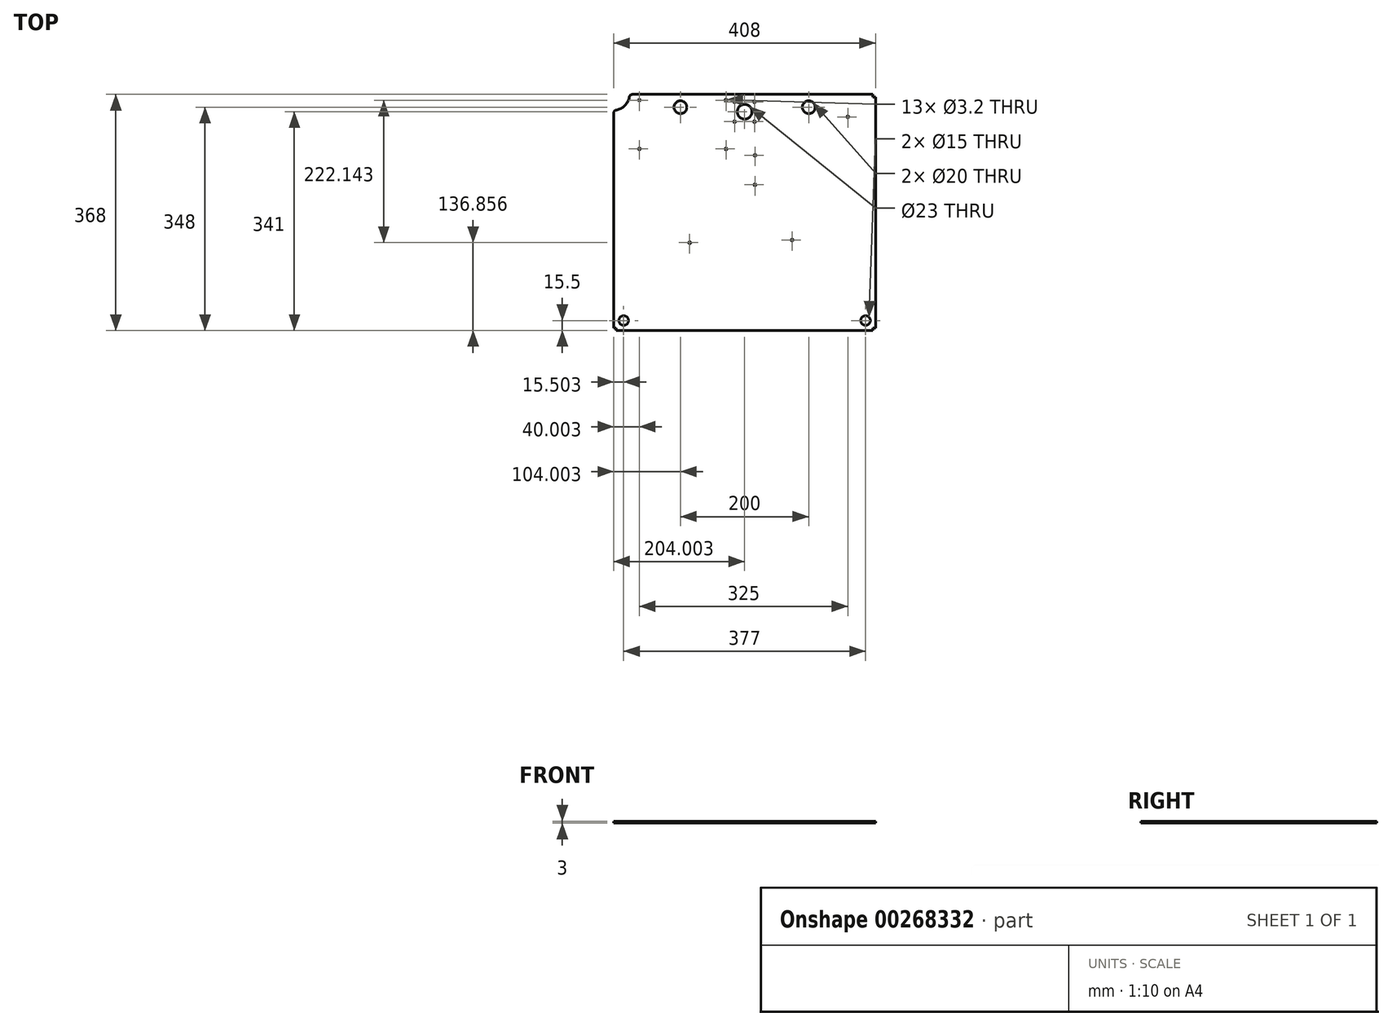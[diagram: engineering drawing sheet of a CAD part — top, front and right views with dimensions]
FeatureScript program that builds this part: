
annotation { "Feature Type Name" : "Feature", "Feature Type Description" : "" }
export const myFeature = defineFeature(function(context is Context, id is Id, definition is map)
    precondition{}
    {
        {
            var Q0;
            Q0=qCreatedBy(makeId("Top.planeOp"),FACE);
            var sketch = newSketch(context, id + "F0", { "sketchPlane" : qUnion([Q0])});
            skLineSegment(sketch, "E0.bottom", {"start": v(-284.09, 364.84) * mm, "end": v(90.72, 364.84) * mm});
            skLineSegment(sketch, "E0.top", {"start": v(-309.28, -3.16) * mm, "end": v(90.72, -3.16) * mm});
            skLineSegment(sketch, "E0.left", {"start": v(-313.28, 335.68) * mm, "end": v(-313.28, 0.84) * mm});
            skLineSegment(sketch, "E0.right", {"start": v(94.72, 360.84) * mm, "end": v(94.72, 0.84) * mm});
            skLineSegment(sketch, "E1", {"start": v(90.72, 364.84) * mm, "end": v(90.72, 360.84) * mm});
            skLineSegment(sketch, "E2", {"start": v(90.72, 360.84) * mm, "end": v(94.72, 360.84) * mm});
            skLineSegment(sketch, "E3", {"start": v(94.72, 0.84) * mm, "end": v(90.72, 0.84) * mm});
            skLineSegment(sketch, "E4", {"start": v(90.72, 0.84) * mm, "end": v(90.72, -3.16) * mm});
            skLineSegment(sketch, "E5", {"start": v(-313.28, 0.84) * mm, "end": v(-309.28, 0.84) * mm});
            skLineSegment(sketch, "E6", {"start": v(-309.28, 0.84) * mm, "end": v(-309.28, -3.16) * mm});
            skPoint(sketch, "E7.orphan", {"position": v(94.72, 364.84) * mm});
            skArc(sketch, "E8", {"start": v(-309.13, 340.6) * mm, "mid": v(-295.89, 347.46) * mm, "end": v(-289.02, 360.7) * mm});
            skPoint(sketch, "E9.start.orphan", {"position": v(-309.28, 360.84) * mm});
            skPoint(sketch, "E10.visualSharp", {"position": v(-288.65, 364.84) * mm});
            skArc(sketch, "E10.filletArc", {"start": v(-284.09, 364.84) * mm, "mid": v(-287.3, 363.67) * mm, "end": v(-289.02, 360.7) * mm});
            skPoint(sketch, "E11.visualSharp", {"position": v(-313.28, 340.25) * mm});
            skArc(sketch, "E11.filletArc", {"start": v(-309.13, 340.6) * mm, "mid": v(-312.1, 338.9) * mm, "end": v(-313.28, 335.68) * mm});
            skLineSegment(sketch, "E12", {"start": v(-326.8, 180.84) * mm, "end": v(113.22, 180.84) * mm, "construction": true});
            skLineSegment(sketch, "E13", {"start": v(-109.28, 377.2) * mm, "end": v(-109.28, -21.77) * mm, "construction": true});
            skCircle(sketch, "E14", {"center": v(-109.28, 337.84) * mm, "radius": 11.5 * mm});
            skCircle(sketch, "E15", {"center": v(-93.78, 353.34) * mm, "radius": 1.6 * mm});
            skCircle(sketch, "E16", {"center": v(-93.78, 322.34) * mm, "radius": 1.6 * mm});
            skCircle(sketch, "E17", {"center": v(-124.78, 322.34) * mm, "radius": 1.6 * mm});
            skCircle(sketch, "E18", {"center": v(-124.78, 353.34) * mm, "radius": 1.6 * mm});
            skCircle(sketch, "E19", {"center": v(-209.28, 344.84) * mm, "radius": 10 * mm});
            skCircle(sketch, "E20", {"center": v(-9.28, 344.84) * mm, "radius": 10 * mm});
            skCircle(sketch, "E21", {"center": v(-297.78, 12.34) * mm, "radius": 7.5 * mm});
            skCircle(sketch, "E22", {"center": v(79.22, 12.34) * mm, "radius": 7.5 * mm});
            skLineSegment(sketch, "E23.bottom", {"start": v(-273.28, 355.84) * mm, "end": v(-138.28, 355.84) * mm, "construction": true});
            skLineSegment(sketch, "E23.top", {"start": v(-273.28, 279.84) * mm, "end": v(-138.28, 279.84) * mm, "construction": true});
            skLineSegment(sketch, "E23.left", {"start": v(-273.28, 355.84) * mm, "end": v(-273.28, 279.84) * mm, "construction": true});
            skLineSegment(sketch, "E23.right", {"start": v(-138.28, 355.84) * mm, "end": v(-138.28, 279.84) * mm, "construction": true});
            skCircle(sketch, "E24", {"center": v(-273.28, 355.84) * mm, "radius": 1.6 * mm});
            skCircle(sketch, "E25", {"center": v(-273.28, 279.84) * mm, "radius": 1.6 * mm});
            skCircle(sketch, "E26", {"center": v(-138.28, 279.84) * mm, "radius": 1.6 * mm});
            skCircle(sketch, "E27", {"center": v(-138.28, 355.84) * mm, "radius": 1.6 * mm});
            skLineSegment(sketch, "E28.bottom", {"start": v(-35.28, 329.84) * mm, "end": v(51.72, 329.84) * mm, "construction": true});
            skLineSegment(sketch, "E28.top", {"start": v(-35.28, 137.84) * mm, "end": v(51.72, 137.84) * mm, "construction": true});
            skLineSegment(sketch, "E28.left", {"start": v(-35.28, 329.84) * mm, "end": v(-35.28, 137.84) * mm, "construction": true});
            skLineSegment(sketch, "E28.right", {"start": v(51.72, 329.84) * mm, "end": v(51.72, 137.84) * mm, "construction": true});
            skCircle(sketch, "E29", {"center": v(51.72, 329.84) * mm, "radius": 1.6 * mm});
            skCircle(sketch, "E30", {"center": v(-35.28, 137.84) * mm, "radius": 1.6 * mm});
            skLineSegment(sketch, "E31.bottom", {"start": v(-115.57, 276.38) * mm, "end": v(-70.57, 276.38) * mm, "construction": true});
            skLineSegment(sketch, "E31.top", {"start": v(-115.57, 214.38) * mm, "end": v(-70.57, 214.38) * mm, "construction": true});
            skLineSegment(sketch, "E31.left", {"start": v(-115.57, 276.38) * mm, "end": v(-115.57, 214.38) * mm, "construction": true});
            skLineSegment(sketch, "E31.right", {"start": v(-70.57, 276.38) * mm, "end": v(-70.57, 214.38) * mm, "construction": true});
            skLineSegment(sketch, "E32", {"start": v(-93.07, 276.38) * mm, "end": v(-93.07, 214.38) * mm, "construction": true});
            skCircle(sketch, "E33", {"center": v(-93.07, 269.88) * mm, "radius": 1.6 * mm});
            skCircle(sketch, "E34", {"center": v(-93.07, 223.88) * mm, "radius": 1.6 * mm});
            skCircle(sketch, "E35", {"center": v(-194.94, 133.7) * mm, "radius": 1.6 * mm});
            skSolve(sketch);
        }
        {
            var Q0;
            Q0=qSketchRegion(id+"F0",true);
            extrude(context, id + "F1", {"entities" : qUnion([Q0]), "depth" : 3 * mm});
        }
    });
